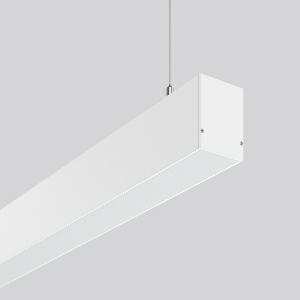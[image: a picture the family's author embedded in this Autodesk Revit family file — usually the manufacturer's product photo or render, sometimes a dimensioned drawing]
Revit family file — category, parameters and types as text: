
# Revit family: less_is_more_50_312313_002_1_930b
name_source: partatom
category: Lighting Fixtures
units: mm (PartAtom-declared; Revit-internal decimal feet)

## family parameters
Cut with Voids When Loaded = No
Host = Face
Light Source = No
Part Type = Normal
Room Calculation Point = No
Round Connector Dimension = Use Diameter
Shared = No

## types (1)
- LESS IS MORE 50 (1 x LED Modul 840, 4050 lm, 4000)
    Apparent Load = 34 VA
    CIE Flux Codes = 48 79 95 100 100
    Color Rendering = 80
    Color Temperature = 4000
    Default Elevation = 1800 mm
    Description = Series: LESS IS MORE 50
Linear pendant luminaire for aesthetically sophisticated lighting. Housing: extruded aluminium profile, powder-coated. End cap aluminium powder-coated. Canopy made of aluminium, powder-coated. Diffuser made of non-yellowing plastic (PMMA), opal. Direct light emission. Suitable for pendant. 2-point steel cable suspension freely positionable and infinitely height-adjustable. Special lengths available on request. LED unit with integrated converter interchangeable and removable. Suitable for through-wiring. With sensors or as a safety luminaire on request. 
Colour: traffic white, matt (RAL 9016)
Length: 1407 mm
Width: 57 mm
Height: 75 mm
Suspension length: 2000 mm
Lamp: LED
Socket: without socket
Colour temperature: 4000K
Colour rendering index (CRI): 80
System power: 34 W
Rated luminous flux: 4050 lm
Luminous efficiency: 119 lm/W
Control gear: Regulated power supply
Protection class: I
Type of protection: IP 20
    Height = 75 mm
    Lamp = 1 x LED Modul 840
    Lamp Light Flux = 4050 lm
    Lamp count = 1
    Length = 1407 mm
    Lifetime = 50000 h
    Luminous efficacy = 119 lm/W
    Manufacturer = RZB
    ModVariant = No
    Model = 312313.002.1
    Mounting Place = Ceiling
    Mounting Type = Pendant
    Number of Poles = 1
    OnlyDefault = Yes
    Power Factor = 1
    Product Name = LESS IS MORE 50
    Product group = Pendant LED linear luminaires
    ProductGroupID = 907
    Protection Class = Protection class I
    Protection Degree = IP 20
    RLX_Detail_Level = 1
    RLX_Emergency_Light_Flux = 0 lm
    RLX_Emergency_Type = 0
    RLX_Emergency_Type_DB = No
    RlxData = <blob elided: 20625 chars, md5=39801216>
    Socket = socket
    Standby Power = 0 W
    System Light Flux = 4050 lm
    System Power = 34 W
    Type Comments = Product without accessories
    Type Image = 312318.002.jpg
    URL = http://relux.com
    VarID = ---
    Voltage = 230 V
    Voltage Range = 220-240 V
    Weight = 0.00 kg
    Width = 57 mm

## geometry (parser evidence)
native form markers: Blend x4, Sweep x10
no freeform markers — native parametric forms only
